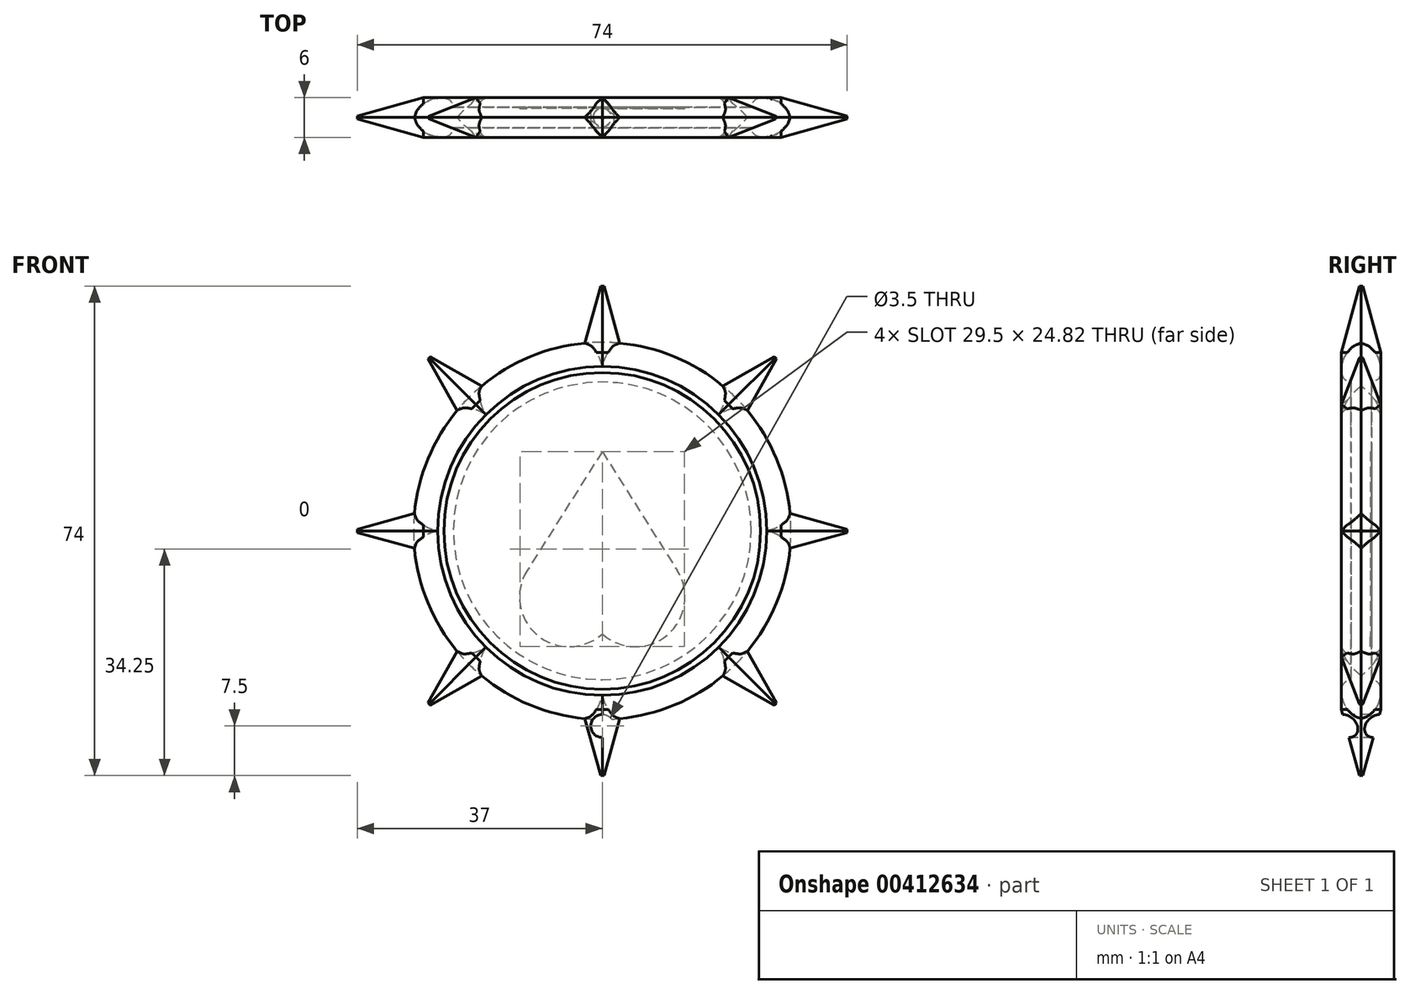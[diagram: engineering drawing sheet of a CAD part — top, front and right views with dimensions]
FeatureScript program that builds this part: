
annotation { "Feature Type Name" : "Feature", "Feature Type Description" : "" }
export const myFeature = defineFeature(function(context is Context, id is Id, definition is map)
    precondition{}
    {
        {
            var Q0;
            Q0=qCreatedBy(makeId("Right.planeOp"),FACE);
            var sketch = newSketch(context, id + "F0", { "sketchPlane" : qUnion([Q0])});
            skLineSegment(sketch, "E0.left", {"start": v(3, 24.86) * mm, "end": v(3, 23.93) * mm});
            skLineSegment(sketch, "E0.right", {"start": v(-3, 24.86) * mm, "end": v(-3, 23.93) * mm});
            skFitSpline(sketch, "E1", {"points": [v(3, 23.93) * mm, v(2.55, 22.95) * mm, v(1.56, 22.5) * mm], "startDerivative": vector(-0.64, -2.23) * mm, "endDerivative": vector(-2.24, -0.64) * mm});
            skFitSpline(sketch, "E2.MirrorCS", {"points": [v(-3, 23.93) * mm, v(-2.55, 22.95) * mm, v(-1.56, 22.5) * mm], "startDerivative": vector(0.64, -2.23) * mm, "endDerivative": vector(2.24, -0.64) * mm});
            skFitSpline(sketch, "E3", {"points": [v(3, 24.86) * mm, v(2.72, 25.8) * mm, v(2.42, 26.5) * mm, v(2.04, 27.08) * mm, v(1.54, 27.6) * mm, v(1.1, 28) * mm, v(0, 28.5) * mm], "startDerivative": vector(-1.48, 5.35) * mm, "endDerivative": vector(-6.13, 2.4) * mm});
            skFitSpline(sketch, "E4.MirrorCS", {"points": [v(-3, 24.86) * mm, v(-2.72, 25.8) * mm, v(-2.42, 26.5) * mm, v(-2.04, 27.08) * mm, v(-1.54, 27.6) * mm, v(-1.1, 28) * mm, v(0, 28.5) * mm], "startDerivative": vector(1.48, 5.35) * mm, "endDerivative": vector(6.13, 2.4) * mm});
            skPoint(sketch, "E5.orphan", {"position": v(3, 28.5) * mm});
            skPoint(sketch, "E6.orphan", {"position": v(-3, 28.5) * mm});
            skPoint(sketch, "E7.orphan", {"position": v(-3, 25.5) * mm});
            skPoint(sketch, "E8.orphan", {"position": v(3, 25.5) * mm});
            skPoint(sketch, "E9.orphan", {"position": v(-3, 22.5) * mm});
            skPoint(sketch, "E10.orphan", {"position": v(3, 22.5) * mm});
            skLineSegment(sketch, "E11.top", {"start": v(1.56, 0) * mm, "end": v(-1.56, 0) * mm});
            skLineSegment(sketch, "E11.left", {"start": v(1.56, 22.5) * mm, "end": v(1.56, 0) * mm});
            skLineSegment(sketch, "E11.right", {"start": v(-1.56, 22.5) * mm, "end": v(-1.56, 0) * mm});
            skSolve(sketch);
        }
        {
            var Q0;
            Q0=makeQuery(id+"F0.imprint","IMPRINT",FACE,{"disambiguationData":[TD([[makeQuery(id+"F0.imprint","IMPRINT",EDGE,{"derivedFrom":sQuery(id+"F0.wireOp",EDGE,"E0.left")}),-1.0]])]});
            var Q1;
            Q1=sQuery(id+"F0.wireOp",EDGE,"E11.top");
            revolve(context, id + "F1", {"entities" : qUnion([Q0]), "axis" : qUnion([Q1]), "revolveType" : RevolveType.FULL});
        }
        {
            var Q0;
            Q0=qCreatedBy(makeId("Top.planeOp"),FACE);
            cPlane(context, id + "F2", {"entities" : qUnion([Q0]), "cplaneType" : CPlaneType.OFFSET, "offset" : 25 * mm, "oppositeDirection" : true, "width" : 150 * mm, "height" : 150 * mm});
        }
        {
            var Q0;
            Q0=qCreatedBy(id+"F2.planeOp",FACE);
            var sketch = newSketch(context, id + "F3", { "sketchPlane" : qUnion([Q0])});
            skLineSegment(sketch, "E12", {"start": v(-3, 0) * mm, "end": v(0, -3) * mm});
            skLineSegment(sketch, "E13", {"start": v(0, -3) * mm, "end": v(3, 0) * mm});
            skLineSegment(sketch, "E14", {"start": v(3, 0) * mm, "end": v(0, 3) * mm});
            skLineSegment(sketch, "E15", {"start": v(0, 3) * mm, "end": v(-3, 0) * mm});
            skSolve(sketch);
        }
        {
            var Q0;
            Q0 = qSketchRegion(id + "F3", true);
            extrude(context, id + "F4", {"entities" : qUnion([Q0]), "operationType" : NewBodyOperationType.ADD, "oppositeDirection" : true, "depth" : 12 * mm});
        }
        {
            var Q0;
            Q0=makeQuery(id+"F4.opExtrude","CAP_EDGE",EDGE,{"disambiguationData":[OSD([sQuery(id+"F3.wireOp",EDGE,"E14")])],"isStart":false});
            var Q1;
            Q1=makeQuery(id+"F4.opExtrude","CAP_EDGE",EDGE,{"disambiguationData":[OSD([sQuery(id+"F3.wireOp",EDGE,"E15")])],"isStart":false});
            var Q2;
            Q2=makeQuery(id+"F4.opExtrude","CAP_EDGE",EDGE,{"disambiguationData":[OSD([sQuery(id+"F3.wireOp",EDGE,"E12")])],"isStart":false});
            var Q3;
            Q3=makeQuery(id+"F4.opExtrude","CAP_EDGE",EDGE,{"disambiguationData":[OSD([sQuery(id+"F3.wireOp",EDGE,"E13")])],"isStart":false});
            chamfer(context, id + "F5", {"entities" : qUnion([Q0, Q1, Q2, Q3]), "chamferType" : ChamferType.OFFSET_ANGLE, "width" : 10 * mm, "oppositeDirection" : false, "angle" : 11 * degree, "tangentPropagation" : true});
        }
        {
            var Q0;
            Q0=qCreatedBy(makeId("Top.planeOp"),FACE);
            var sketch = newSketch(context, id + "F6", { "sketchPlane" : qUnion([Q0])});
            skLineSegment(sketch, "E16", {"start": v(0, -43.64) * mm, "end": v(0, 47.2) * mm, "construction": true});
            skSolve(sketch);
        }
        {
            var Q0;
            Q0=makeQuery(id+"F1.opRevolve","SWEPT_BODY",BODY,{"disambiguationData":[OSD([sQuery(id+"F0.wireOp",EDGE,"E0.left"),sQuery(id+"F0.wireOp",EDGE,"E0.right"),sQuery(id+"F0.wireOp",EDGE,"E1"),sQuery(id+"F0.wireOp",EDGE,"E2.MirrorCS"),sQuery(id+"F0.wireOp",EDGE,"E3"),sQuery(id+"F0.wireOp",EDGE,"E4.MirrorCS"),sQuery(id+"F0.wireOp",EDGE,"E11.top"),sQuery(id+"F0.wireOp",EDGE,"E11.left"),sQuery(id+"F0.wireOp",EDGE,"E11.right")])]});
            var Q1;
            Q1=sQuery(id+"F6.wireOp",EDGE,"E16");
            circularPattern(context, id + "F7", {"entities" : qUnion([Q0]), "axis" : qUnion([Q1]), "angle" : 360 * degree, "instanceCount" : 8, "equalSpace" : true});
        }
        {
            var Q0;
            Q0=qCreatedBy(makeId("Front.planeOp"),FACE);
            var sketch = newSketch(context, id + "F8", { "sketchPlane" : qUnion([Q0])});
            skCircle(sketch, "E17", {"center": v(0, -29.5) * mm, "radius": 1.75 * mm});
            skSolve(sketch);
        }
        {
            var Q0;
            Q0 = qSketchRegion(id + "F8", true);
            extrude(context, id + "F9", {"entities" : qUnion([Q0]), "operationType" : NewBodyOperationType.REMOVE, "endBound" : BoundingType.SYMMETRIC, "oppositeDirection" : true, "depth" : 23.6 * mm});
        }
        {
            var Q0;
            Q0=makeQuery(id+"F7.opPattern","COPY",FACE,{"derivedFrom":makeQuery(id+"F1.opRevolve","SWEPT_FACE",FACE,{"disambiguationData":[OSD([sQuery(id+"F0.wireOp",EDGE,"E11.left")])]}),"instanceName":"4"});
            var sketch = newSketch(context, id + "F10", { "sketchPlane" : qUnion([Q0])});
            skArc(sketch, "E18", {"start": v(0, -15.6) * mm, "mid": v(9.84, -15.73) * mm, "end": v(11.35, -6) * mm});
            skLineSegment(sketch, "E19", {"start": v(0, -33.05) * mm, "end": v(0, 14.34) * mm, "construction": true});
            skLineSegment(sketch, "E20", {"start": v(0, 12) * mm, "end": v(11.35, -6) * mm});
            skArc(sketch, "E21.MirrorCS", {"start": v(0, -15.6) * mm, "mid": v(-9.84, -15.73) * mm, "end": v(-11.35, -6) * mm});
            skLineSegment(sketch, "E22.MirrorCS", {"start": v(0, 12) * mm, "end": v(-11.35, -6) * mm});
            skSolve(sketch);
        }
        {
            var Q0;
            Q0=makeQuery(id+"F10.imprint","IMPRINT",FACE,{"disambiguationData":[TD([[makeQuery(id+"F10.imprint","IMPRINT",EDGE,{"derivedFrom":sQuery(id+"F10.wireOp",EDGE,"E18")}),1.0]])]});
            extrude(context, id + "F11", {"entities" : qUnion([Q0]), "operationType" : NewBodyOperationType.REMOVE, "oppositeDirection" : true, "depth" : .2 * mm});
        }
    });
